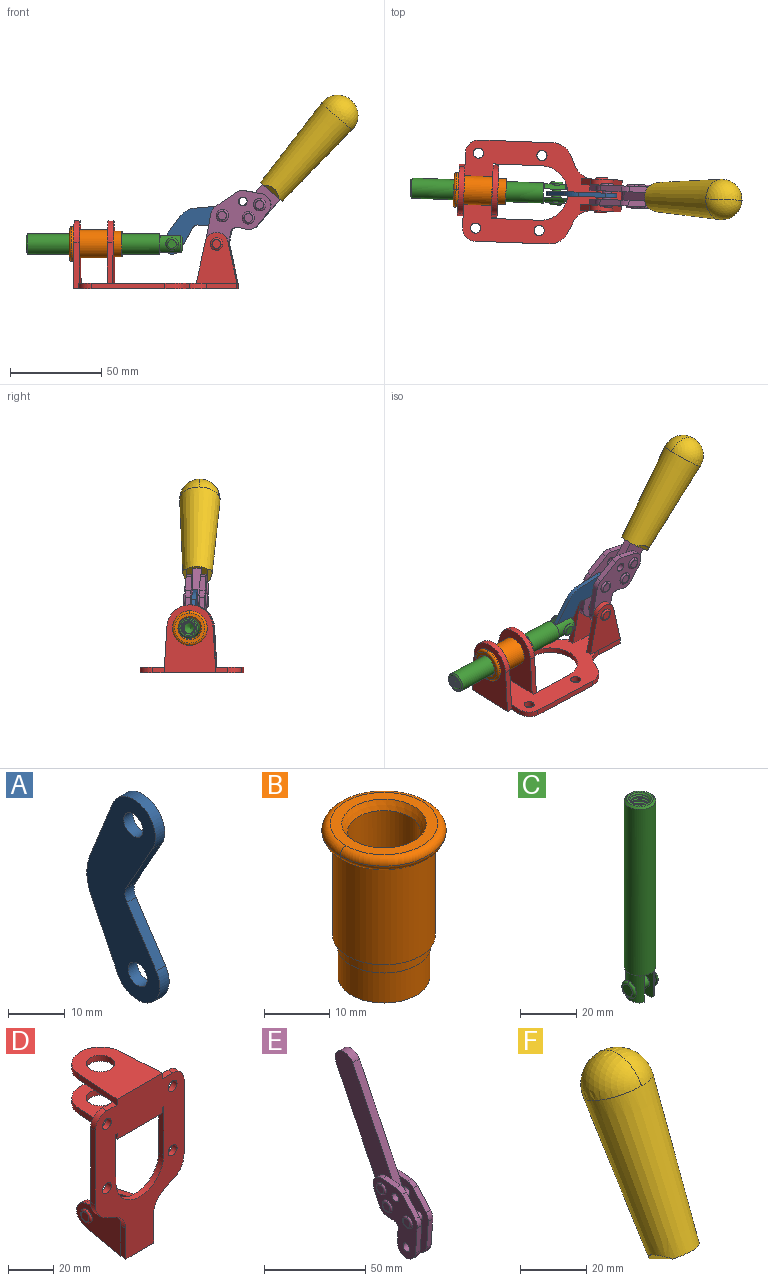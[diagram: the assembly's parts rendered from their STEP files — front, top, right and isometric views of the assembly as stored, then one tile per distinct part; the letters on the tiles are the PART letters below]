
ASSEMBLY  parts=6 mates=7
PART A: 12 faces, bbox 2.3x18.2x42.8 mm
  f0: cylinder r=2.4mm len=4.8mm, axis (1,0,0), area 34.9mm2, adj f4,f11
  f1: cylinder r=10.41mm len=8.47mm, axis (1,0,0), area 20.2mm2, adj f4,f9,f10,f11
  f2: cylinder r=3.05mm len=3.16mm, axis (1,0,0), area 7.7mm2, adj f4,f6,f7,f11
  f3: cylinder r=2.4mm len=4.8mm, axis (1,0,0), area 34.9mm2, adj f4,f11
  f4: plane 42.81x18.23mm, normal (-1,0,0), area 414.1mm2, adj f0,f1,f2,f3,f5,f6,f7,f8
  f5: cylinder r=5.54mm len=10.67mm, axis (1,0,0), area 41.8mm2, adj f4,f6,f10,f11
  f6: plane 11.66x6.53mm, normal (0,-0.87,-0.49), area 30.9mm2, adj f2,f4,f5,f11
  f7: plane 11.17x7.33mm, normal (0,-0.84,0.55), area 30.9mm2, adj f2,f4,f8,f11
  f8: cylinder r=5.54mm len=10.51mm, axis (1,0,0), area 41.8mm2, adj f4,f7,f9,f11
  f9: plane 13.67x6.67mm, normal (0,0.9,-0.44), area 35.1mm2, adj f1,f4,f8,f11
  f10: plane 14.1x5.7mm, normal (0,0.93,0.37), area 35.1mm2, adj f1,f4,f5,f11
  f11: plane 42.81x18.23mm, normal (1,0,0), area 414.1mm2, adj f0,f1,f2,f3,f5,f6,f7,f8
PART B: 15 faces, bbox 20.6x20.6x28.7 mm
  f0: torus R=8.26mm, axis (0,0,1), area 56.8mm2, adj f1,f10,f12
  f1: torus R=8.26mm, axis (0,0,1), area 56.8mm2, adj f0,f6,f13
  f2: cylinder r=5.59mm len=25.91mm, axis (0,0,1), area 909.6mm2, adj f3,f4
  f3: cone r=6.86mm half-angle=45deg, axis (0,0,-1), area 70.2mm2, adj f2,f14
  f4: cone r=6.47mm half-angle=30deg, axis (0,0,1), area 66.7mm2, adj f2,f13
  f5: cylinder r=7.04mm len=14.07mm, axis (0,0,1), area 252.6mm2, adj f11,f14
  f6: torus R=8.26mm, axis (0,0,1), area 56.8mm2, adj f1,f12,f13
  f7: cylinder r=7.16mm len=14.33mm, axis (0,0,1), area 91.5mm2, adj f9,f11
  f8: cylinder r=7.86mm len=18.42mm, axis (0,0,1), area 909.6mm2, adj f9,f10
  f9: plane 15.72x15.72mm, normal (0,0,-1), area 33mm2, adj f7,f8
  f10: plane 16.51x16.51mm, normal (0,0,-1), area 19.9mm2, adj f0,f8,f12
  f11: plane 14.33x14.33mm, normal (0,0,-1), area 5.7mm2, adj f5,f7
  f12: torus R=8.26mm, axis (0,0,1), area 56.8mm2, adj f0,f6,f10
  f13: plane 16.51x16.51mm, normal (0,0,1), area 82.7mm2, adj f1,f4,f6
  f14: plane 14.07x14.07mm, normal (0,0,-1), area 7.8mm2, adj f3,f5
PART C: 48 faces, bbox 12.6x11.1x86.1 mm
  f0: torus R=2.41mm, axis (-1,0,0), area 15mm2, adj f30,f32,f34
  f1: torus R=2.41mm, axis (-1,0,0), area 15mm2, adj f29,f31,f33
  f2: cylinder r=5.54mm len=72.39mm, axis (0,0,1), area 2518.5mm2, adj f3,f4,f42,f43
  f3: cone r=5.54mm half-angle=45deg, axis (0,0,1), area 7.6mm2, adj f2,f5,f41
  f4: cone r=5.54mm half-angle=45deg, axis (0,0,-1), area 34.9mm2, adj f2,f39
  f5: cylinder r=5.08mm len=11.48mm, axis (0,0,1), area 108.3mm2, adj f3,f7,f8,f41
  f6: cylinder r=2.41mm len=4.83mm, axis (-1,0,0), area 71.2mm2, adj f40,f41
  f7: cylinder r=2.41mm len=4.83mm, axis (-1,0,0), area 7.6mm2, adj f5,f34
  f8: cone r=5.08mm half-angle=45deg, axis (0,0,1), area 10.6mm2, adj f5,f37,f41
  f9: cone r=3.98mm half-angle=45deg, axis (0,0,1), area 17.6mm2, adj f27,f39,f45,f46,f47
  f10: cylinder r=2.41mm len=4.83mm, axis (-1,0,0), area 7.6mm2, adj f33,f38
  f11: cylinder r=3.2mm len=6.4mm, axis (0,0,1), area 78.4mm2, adj f12,f28,f44,f45,f47
  f12: cylinder r=3.2mm len=6.4mm, axis (0,0,1), area 10.5mm2, adj f11,f13,f45,f47
  f13: cylinder r=3.2mm len=6.4mm, axis (0,0,1), area 10.5mm2, adj f12,f14,f45,f47
  f14: cylinder r=3.2mm len=6.4mm, axis (0,0,1), area 10.5mm2, adj f13,f15,f45,f47
  f15: cylinder r=3.2mm len=6.4mm, axis (0,0,1), area 10.5mm2, adj f14,f16,f45,f47
  f16: cylinder r=3.2mm len=6.4mm, axis (0,0,1), area 10.5mm2, adj f15,f17,f45,f47
  f17: cylinder r=3.2mm len=6.4mm, axis (0,0,1), area 10.5mm2, adj f16,f18,f45,f47
  f18: cylinder r=3.2mm len=6.4mm, axis (0,0,1), area 10.5mm2, adj f17,f19,f45,f47
  f19: cylinder r=3.2mm len=6.4mm, axis (0,0,1), area 10.5mm2, adj f18,f20,f45,f47
  f20: cylinder r=3.2mm len=6.4mm, axis (0,0,1), area 10.5mm2, adj f19,f21,f45,f47
  f21: cylinder r=3.2mm len=6.4mm, axis (0,0,1), area 10.5mm2, adj f20,f22,f45,f47
  f22: cylinder r=3.2mm len=6.4mm, axis (0,0,1), area 10.5mm2, adj f21,f23,f45,f47
  f23: cylinder r=3.2mm len=6.4mm, axis (0,0,1), area 10.5mm2, adj f22,f24,f45,f47
  f24: cylinder r=3.2mm len=6.4mm, axis (0,0,1), area 10.5mm2, adj f23,f25,f45,f47
  f25: cylinder r=3.2mm len=6.4mm, axis (0,0,1), area 10.5mm2, adj f24,f26,f45,f47
  f26: cylinder r=3.2mm len=6.4mm, axis (0,0,1), area 10.5mm2, adj f25,f27,f45,f47
  f27: cylinder r=3.2mm len=6.4mm, axis (0,0,1), area 7.4mm2, adj f9,f26,f45,f47
  f28: cone r=3.2mm half-angle=60deg, axis (0,0,1), area 37.2mm2, adj f11
  f29: plane 4.83x4.83mm, normal (-1,0,0), area 18.3mm2, adj f1,f31
  f30: plane 4.83x4.83mm, normal (1,0,0), area 18.3mm2, adj f0,f32
  f31: torus R=2.41mm, axis (-1,0,0), area 15mm2, adj f1,f29,f33
  f32: torus R=2.41mm, axis (-1,0,0), area 15mm2, adj f0,f30,f34
  f33: plane 6.83x6.83mm, normal (1,0,0), area 18.3mm2, adj f1,f10,f31
  f34: plane 6.83x6.83mm, normal (-1,0,0), area 18.3mm2, adj f0,f7,f32
  f35: cone r=5.08mm half-angle=45deg, axis (0,0,1), area 10.6mm2, adj f36,f38,f40
  f36: plane 7.25x1.97mm, normal (0,0,-1), area 10mm2, adj f35,f40
  f37: plane 7.25x1.97mm, normal (0,0,-1), area 10mm2, adj f8,f41
  f38: cylinder r=5.08mm len=11.48mm, axis (0,0,1), area 108.3mm2, adj f10,f35,f40,f42
  f39: plane 9.55x9.55mm, normal (0,0,1), area 22mm2, adj f4,f9
  f40: plane 12.76x10.09mm, normal (1,0,0), area 95.7mm2, adj f6,f35,f36,f38,f42,f43
  f41: plane 12.76x10.09mm, normal (-1,0,0), area 95.7mm2, adj f3,f5,f6,f8,f37,f43
  f42: cone r=5.54mm half-angle=45deg, axis (0,0,1), area 7.6mm2, adj f2,f38,f40
  f43: plane 11.07x4.7mm, normal (0,0,-1), area 50.4mm2, adj f2,f40,f41
  f44: plane 0.89x0.62mm, normal (-1,0,0), area 0.3mm2, adj f11,f45,f46,f47
  f45: bspline ~24.8x7.63mm, area 266.6mm2, adj f9,f11,f12,f13,f14,f15,f16,f17
  f46: bspline ~24.87x7.63mm, area 73.6mm2, adj f9,f44,f45,f47
  f47: bspline ~24.98x7.63mm, area 272.5mm2, adj f9,f11,f12,f13,f14,f15,f16,f17
PART D: 55 faces, bbox 55.7x37.4x89.8 mm
  f0: torus R=2.41mm, axis (-1,0,0), area 15mm2, adj f11,f15,f25
  f1: torus R=2.41mm, axis (-1,0,0), area 15mm2, adj f10,f12,f22
  f2: cylinder r=2.78mm len=5.56mm, axis (0,-1,0), area 54.2mm2, adj f30,f54
  f3: cylinder r=14.99mm len=29.97mm, axis (0,-1,0), area 145.9mm2, adj f30,f49,f53,f54
  f4: cylinder r=2.78mm len=5.56mm, axis (0,-1,0), area 54.2mm2, adj f30,f54
  f5: cylinder r=2.78mm len=5.56mm, axis (0,-1,0), area 54.2mm2, adj f30,f54
  f6: cylinder r=2.78mm len=5.56mm, axis (0,-1,0), area 54.2mm2, adj f30,f54
  f7: cylinder r=6.35mm len=12.7mm, axis (0,0,1), area 123.6mm2, adj f27,f51
  f8: cylinder r=6.35mm len=12.7mm, axis (0,0,-1), area 124.7mm2, adj f21,f35
  f9: cylinder r=2.41mm len=11.18mm, axis (-1,0,0), area 169.4mm2, adj f16,f19
  f10: plane 4.83x4.83mm, normal (1,0,0), area 18.3mm2, adj f1,f12
  f11: plane 4.83x4.83mm, normal (-1,0,0), area 18.3mm2, adj f0,f15
  f12: torus R=2.41mm, axis (-1,0,0), area 15mm2, adj f1,f10,f22
  f13: cylinder r=6.35mm len=12.41mm, axis (1,0,0), area 53.4mm2, adj f18,f19,f22,f23
  f14: cylinder r=6.35mm len=12.41mm, axis (-1,0,0), area 53.4mm2, adj f16,f17,f24,f25
  f15: torus R=2.41mm, axis (-1,0,0), area 15mm2, adj f0,f11,f25
  f16: plane 27.86x22.35mm, normal (1,0,0), area 425.4mm2, adj f9,f14,f17,f24,f30
  f17: plane 22.86x4.97mm, normal (0,0.21,0.98), area 72.5mm2, adj f14,f16,f25,f30
  f18: plane 22.86x4.97mm, normal (0,0.21,0.98), area 72.5mm2, adj f13,f19,f22,f30
  f19: plane 27.86x22.35mm, normal (-1,0,0), area 425.4mm2, adj f9,f13,f18,f23,f30
  f20: cylinder r=12.7mm len=25.35mm, axis (0,0,-1), area 119.8mm2, adj f21,f34,f35,f36
  f21: plane 34.21x28.07mm, normal (0,0,-1), area 702.4mm2, adj f8,f20,f30,f34,f36
  f22: plane 27.96x22.45mm, normal (1,0,0), area 407.2mm2, adj f1,f12,f13,f18,f23,f30,f42,f43
  f23: plane 22.86x4.97mm, normal (0,0.21,-0.98), area 72.5mm2, adj f13,f19,f22,f44
  f24: plane 22.86x4.97mm, normal (0,0.21,-0.98), area 72.5mm2, adj f14,f16,f25,f44
  f25: plane 27.86x22.35mm, normal (-1,0,0), area 407.1mm2, adj f0,f14,f15,f17,f24,f30,f45,f46
  f26: plane 3.1x0.95mm, normal (0,0,-1), area 2.7mm2, adj f30,f49,f50,f54
  f27: plane 34.21x28.07mm, normal (0,0,1), area 702.4mm2, adj f7,f28,f30,f50,f52
  f28: cylinder r=12.7mm len=25.35mm, axis (0,0,1), area 118.8mm2, adj f27,f50,f51,f52
  f29: plane 3.1x0.95mm, normal (0,0,-1), area 2.7mm2, adj f30,f52,f53,f54
  f30: plane 86.54x55.63mm, normal (0,1,0), area 2362.9mm2, adj f2,f3,f4,f5,f6,f16,f17,f18
  f31: plane 40.56x3.1mm, normal (-1,0,0), area 125.7mm2, adj f30,f32,f48,f54
  f32: cylinder r=7.11mm len=7.11mm, axis (0,-1,0), area 34.6mm2, adj f30,f31,f33,f54
  f33: plane 6.67x3.1mm, normal (0,0,1), area 20.4mm2, adj f30,f32,f34,f54
  f34: plane 25.39x3.13mm, normal (-1,0.06,0), area 79.5mm2, adj f20,f21,f33,f35,f54
  f35: plane 37.31x28.45mm, normal (0,0,1), area 789.9mm2, adj f8,f20,f34,f36,f54
  f36: plane 25.39x3.13mm, normal (1,0.06,0), area 79.5mm2, adj f20,f21,f35,f37,f54
  f37: plane 6.67x3.1mm, normal (0,0,1), area 20.4mm2, adj f30,f36,f38,f54
  f38: cylinder r=7.11mm len=7.11mm, axis (0,-1,0), area 34.6mm2, adj f30,f37,f39,f54
  f39: plane 40.56x3.1mm, normal (1,0,0), area 125.7mm2, adj f30,f38,f40,f54
  f40: cylinder r=11.18mm len=10.16mm, axis (0,-1,0), area 39.5mm2, adj f30,f39,f41,f54
  f41: plane 6.09x3.1mm, normal (0.42,0,-0.91), area 20.8mm2, adj f30,f40,f42,f54
  f42: cylinder r=11.18mm len=9.41mm, axis (0,-1,0), area 37.2mm2, adj f22,f30,f41,f43,f54
  f43: plane 16.5x3.1mm, normal (1,0,0), area 51.1mm2, adj f22,f42,f44,f54
  f44: plane 17.37x3.1mm, normal (0,0,-1), area 53.8mm2, adj f23,f24,f30,f43,f45,f54
  f45: plane 16.5x3.1mm, normal (-1,0,0), area 51.1mm2, adj f25,f44,f46,f54
  f46: cylinder r=11.18mm len=9.41mm, axis (0,-1,0), area 37.2mm2, adj f25,f30,f45,f47,f54
  f47: plane 6.09x3.1mm, normal (-0.42,0,-0.91), area 20.8mm2, adj f30,f46,f48,f54
  f48: cylinder r=11.18mm len=10.16mm, axis (0,-1,0), area 39.5mm2, adj f30,f31,f47,f54
  f49: plane 26.54x3.1mm, normal (-1,0,0), area 82.3mm2, adj f3,f26,f30,f54
  f50: plane 25.39x3.1mm, normal (1,0.06,0), area 78.8mm2, adj f26,f27,f28,f51,f54
  f51: plane 37.31x28.45mm, normal (0,0,-1), area 789.9mm2, adj f7,f28,f50,f52,f54
  f52: plane 25.39x3.1mm, normal (-1,0.06,0), area 78.8mm2, adj f27,f28,f29,f51,f54
  f53: plane 26.54x3.1mm, normal (1,0,0), area 82.3mm2, adj f3,f29,f30,f54
  f54: plane 89.66x55.63mm, normal (0,-1,0), area 2678.5mm2, adj f2,f3,f4,f5,f6,f26,f29,f31
PART E: 59 faces, bbox 12.9x60.2x99.6 mm
  f0: torus R=2.39mm, axis (-1,0,0), area 14.9mm2, adj f20,f43,f51
  f1: torus R=2.39mm, axis (-1,0,0), area 14.9mm2, adj f19,f42,f51
  f2: torus R=2.39mm, axis (-1,0,0), area 14.9mm2, adj f18,f35,f51
  f3: torus R=2.39mm, axis (-1,0,0), area 14.9mm2, adj f14,f17,f23
  f4: torus R=2.39mm, axis (-1,0,0), area 14.9mm2, adj f13,f16,f23
  f5: torus R=2.39mm, axis (-1,0,0), area 14.9mm2, adj f12,f15,f23
  f6: cylinder r=2.39mm len=4.78mm, axis (1,0,0), area 46.5mm2, adj f48,f50,f51
  f7: cylinder r=2.39mm len=4.78mm, axis (1,0,0), area 46.5mm2, adj f50,f51
  f8: cylinder r=6.35mm len=12.68mm, axis (1,0,0), area 61.8mm2, adj f38,f39,f50,f51
  f9: cylinder r=2.39mm len=4.78mm, axis (-1,0,0), area 70.5mm2, adj f46,f50
  f10: cylinder r=2.39mm len=4.78mm, axis (-1,0,0), area 46.5mm2, adj f23,f45,f46
  f11: cylinder r=2.39mm len=4.78mm, axis (-1,0,0), area 46.5mm2, adj f23,f46
  f12: plane 4.78x4.78mm, normal (1,0,0), area 17.9mm2, adj f5,f15
  f13: plane 4.78x4.78mm, normal (1,0,0), area 17.9mm2, adj f4,f16
  f14: plane 4.78x4.78mm, normal (1,0,0), area 17.9mm2, adj f3,f17
  f15: torus R=2.39mm, axis (-1,0,0), area 14.9mm2, adj f5,f12,f23
  f16: torus R=2.39mm, axis (-1,0,0), area 14.9mm2, adj f4,f13,f23
  f17: torus R=2.39mm, axis (-1,0,0), area 14.9mm2, adj f3,f14,f23
  f18: plane 4.78x4.78mm, normal (-1,0,0), area 17.9mm2, adj f2,f35
  f19: plane 4.78x4.78mm, normal (-1,0,0), area 17.9mm2, adj f1,f42
  f20: plane 4.78x4.78mm, normal (-1,0,0), area 17.9mm2, adj f0,f43
  f21: plane 2.26x0.2mm, normal (1,0,0), area 0.2mm2, adj f31,f44
  f22: plane 2.26x0.2mm, normal (-1,0,0), area 0.2mm2, adj f41,f44
  f23: plane 39.37x30.77mm, normal (1,0,0), area 565.5mm2, adj f3,f4,f5,f10,f11,f15,f16,f17
  f24: cylinder r=6.1mm len=4.15mm, axis (-1,0,0), area 14.7mm2, adj f23,f25,f32,f46
  f25: plane 10.25x9.01mm, normal (0,-0.75,0.66), area 42.3mm2, adj f23,f24,f26,f46
  f26: cylinder r=6.35mm len=4.64mm, axis (-1,0,0), area 15.6mm2, adj f23,f25,f27,f46
  f27: plane 15.84x3.1mm, normal (0,-1,-0.07), area 49.2mm2, adj f23,f26,f28,f46
  f28: cylinder r=6.35mm len=12.68mm, axis (-1,0,0), area 61.8mm2, adj f23,f27,f29,f46
  f29: plane 8.11x3.1mm, normal (0,1,0.07), area 25.2mm2, adj f23,f28,f30,f46
  f30: cylinder r=3.05mm len=3.25mm, axis (-1,0,0), area 14.8mm2, adj f23,f29,f31,f46
  f31: plane 5.99x3.1mm, normal (0,0.07,-1), area 18.6mm2, adj f21,f23,f30,f44,f46
  f32: plane 9.5x3.1mm, normal (0,-0.07,1), area 29.5mm2, adj f23,f24,f33,f46,f47
  f33: cylinder r=6.1mm len=8.63mm, axis (-1,0,0), area 39.1mm2, adj f23,f32,f34,f47
  f34: plane 8.65x3.96mm, normal (0,0.91,-0.42), area 29.5mm2, adj f23,f33,f44,f47
  f35: torus R=2.39mm, axis (-1,0,0), area 14.9mm2, adj f2,f18,f51
  f36: plane 10.25x9.01mm, normal (0,-0.75,0.66), area 42.3mm2, adj f37,f49,f50,f51
  f37: cylinder r=6.35mm len=4.64mm, axis (1,0,0), area 15.6mm2, adj f36,f38,f50,f51
  f38: plane 15.84x3.1mm, normal (0,-1,-0.07), area 49.2mm2, adj f8,f37,f50,f51
  f39: plane 8.11x3.1mm, normal (0,1,0.07), area 25.2mm2, adj f8,f40,f50,f51
  f40: cylinder r=3.05mm len=3.25mm, axis (1,0,0), area 14.8mm2, adj f39,f41,f50,f51
  f41: plane 5.99x3.1mm, normal (0,0.07,-1), area 18.6mm2, adj f22,f40,f44,f50,f51
  f42: torus R=2.39mm, axis (-1,0,0), area 14.9mm2, adj f1,f19,f51
  f43: torus R=2.39mm, axis (-1,0,0), area 14.9mm2, adj f0,f20,f51
  f44: cylinder r=6.35mm len=12.12mm, axis (-1,0,0), area 128.9mm2, adj f21,f22,f23,f31,f34,f41,f46,f47
  f45: plane 2.65x1.35mm, normal (1,0,0), area 1mm2, adj f10,f55
  f46: plane 39.08x20.42mm, normal (-1,0,0), area 412.5mm2, adj f9,f10,f11,f24,f25,f26,f27,f28
  f47: plane 77.62x39.82mm, normal (1,0,0), area 850mm2, adj f32,f33,f34,f44,f53,f54,f55
  f48: plane 2.65x1.35mm, normal (-1,0,0), area 1mm2, adj f6,f55
  f49: cylinder r=6.1mm len=4.15mm, axis (1,0,0), area 14.7mm2, adj f36,f50,f51,f56
  f50: plane 39.08x20.42mm, normal (1,0,0), area 412.5mm2, adj f6,f7,f8,f9,f36,f37,f38,f39
  f51: plane 39.37x30.77mm, normal (-1,0,0), area 565.5mm2, adj f0,f1,f2,f6,f7,f8,f35,f36
  f52: plane 8.65x3.96mm, normal (0,0.91,-0.42), area 29.5mm2, adj f44,f51,f57,f58
  f53: plane 68.49x33.4mm, normal (0,0.9,-0.44), area 358.1mm2, adj f44,f47,f54,f58
  f54: cylinder r=6.35mm len=12.06mm, axis (1,0,0), area 93.7mm2, adj f47,f53,f55,f58
  f55: plane 68.49x33.4mm, normal (0,-0.9,0.44), area 358.1mm2, adj f44,f45,f46,f47,f48,f50,f54,f58
  f56: plane 9.5x3.1mm, normal (0,-0.07,1), area 29.5mm2, adj f49,f50,f51,f57,f58
  f57: cylinder r=6.1mm len=8.63mm, axis (1,0,0), area 39.1mm2, adj f51,f52,f56,f58
  f58: plane 77.62x39.82mm, normal (-1,0,0), area 850mm2, adj f44,f52,f53,f54,f55,f56,f57
PART F: 11 faces, bbox 22.3x42.6x64.5 mm
  f0: sphere r=11.13mm, area 411.4mm2, adj f1,f8
  f1: cone r=11.11mm half-angle=3.3deg, axis (0,0.44,0.9), area 3251.8mm2, adj f0,f7,f8,f9,f10
  f2: cylinder r=6.16mm len=11.7mm, axis (1,0,0), area 89.5mm2, adj f3,f4,f5,f6
  f3: plane 60.23x36.75mm, normal (-1,0,0), area 763.6mm2, adj f2,f4,f6,f10
  f4: plane 51.37x25.05mm, normal (0,0.9,-0.44), area 264.2mm2, adj f2,f3,f5,f10
  f5: plane 60.23x36.75mm, normal (1,0,0), area 763.6mm2, adj f2,f4,f6,f10
  f6: plane 51.37x25.05mm, normal (0,-0.9,0.44), area 264.2mm2, adj f2,f3,f5,f10
  f7: plane 9.95x5.95mm, normal (0.71,-0.31,-0.64), area 25.8mm2, adj f1,f10
  f8: sphere r=11.13mm, area 411.4mm2, adj f0,f1
  f9: plane 9.95x5.95mm, normal (-0.71,-0.31,-0.64), area 25.8mm2, adj f1,f10
  f10: plane 14.27x11.38mm, normal (0,-0.44,-0.9), area 106.7mm2, adj f1,f3,f4,f5,f6,f7,f9
PLACE A rot(axis=(0.47,0.46,0.75),104deg) t=(32.69,-1.22,11.22)mm
PLACE B rot(axis=(-0.02,-1,-0.02),90deg) t=(-0.92,-24.6,24.61)mm
PLACE C rot(axis=(0.56,-0.58,-0.58),121.2deg) t=(22.92,-0.85,0)mm
PLACE D rot(axis=(0.56,-0.58,-0.58),121.2deg) t=(0,0,0)mm fixed
PLACE E rot(axis=(-0.12,0.13,-0.98),93.1deg) t=(16.61,-0.62,61.98)mm
PLACE F rot(axis=(-0.12,0.13,-0.98),93.1deg) t=(16.61,-0.66,61.98)mm
MATE cylindrical B.f2 <-> D.f7  axis (-1,0.04,0) through (-48.9,1.82,24.61)mm
MATE fastened D.f7 <-> B.f2  axis (-1,0.04,0) through (-46.36,1.73,24.61)mm
MATE cylindrical A.f3 <-> C.f6  axis (0.04,1,0) through (7.5,0.88,24.61)mm
MATE fastened F.f2 <-> E.f54  axis (0.04,1,0) through (99.26,-6.05,96.5)mm
MATE cylindrical C.f2 <-> B.f2  axis (-1,0.04,0) through (-35.82,1.34,24.61)mm
MATE revolute E.f7 <-> D.f0  axis (-0.04,-1,0) through (32.07,-1.2,24.61)mm
MATE revolute A.f5 <-> E.f4  axis (0.04,1,0) through (35.1,-1.31,40.2)mm
